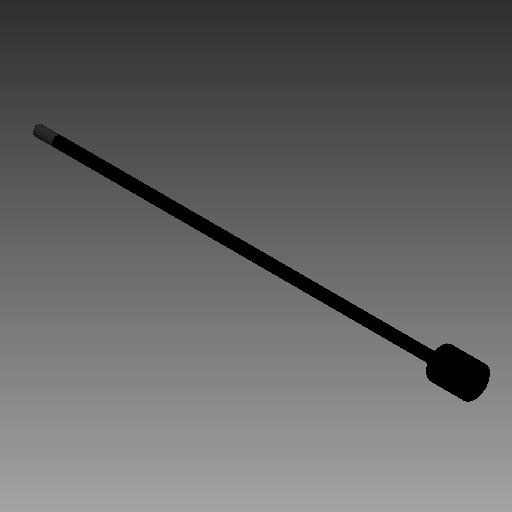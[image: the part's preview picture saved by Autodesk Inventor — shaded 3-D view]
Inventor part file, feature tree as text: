
AUTODESK INVENTOR PART (.ipt)
format: ipt  version: 2019.4 (Build 234330000, 330)  size: 141,312 bytes
history: native  units: in
note: dims shown in document units (in); Inventor stores cm internally (conversion verified against a paired STEP export)
features: other x70, revolve x3, sketch x3, thread x1
ambient origin geometry x8: Origin, YZ Plane, XZ Plane, XY Plane, X Axis, Y Axis, Z Axis, Center Point
bodies: Solid1 (feature_tree)
feature tree (77):
  revolve  "Revolution1"  Angle=360.0deg
  revolve  "Revolution2"  Angle=360.0deg
  thread  "Thread1"  [1 undecoded]
  revolve  "Revolution3"  [1 undecoded]
  other  "dia1_XY"
  other  "dia1_YZ"
  other  "dia1_ZX"
  other  "dia1_X"
  other  "dia1_Y"
  other  "dia1_Z"
  other  "dia1_Center"
  other  "dia12_XY"
  other  "dia12_YZ"
  other  "dia12_ZX"
  other  "dia12_X"
  other  "dia12_Y"
  other  "dia12_Z"
  other  "dia12_Center"
  other  "dia2_XY"
  other  "dia2_YZ"
  other  "dia2_ZX"
  other  "dia2_X"
  other  "dia2_Y"
  other  "dia2_Z"
  other  "dia2_Center"
  other  "dia22_XY"
  other  "dia22_YZ"
  other  "dia22_ZX"
  other  "dia22_X"
  other  "dia22_Y"
  other  "dia22_Z"
  other  "dia22_Center"
  other  "rl1_XY"
  other  "rl1_YZ"
  other  "rl1_ZX"
  other  "rl1_X"
  other  "rl1_Y"
  other  "rl1_Z"
  other  "rl1_Center"
  other  "rl2_XY"
  other  "rl2_YZ"
  other  "rl2_ZX"
  other  "rl2_X"
  other  "rl2_Y"
  other  "rl2_Z"
  other  "rl2_Center"
  other  "rod_cp_XY"
  other  "rod_cp_YZ"
  other  "rod_cp_ZX"
  other  "rod_cp_X"
  other  "rod_cp_Y"
  other  "rod_cp_Z"
  other  "rod_cp_Center"
  other  "thd1_XY"
  other  "thd1_YZ"
  other  "thd1_ZX"
  other  "thd1_X"
  other  "thd1_Y"
  other  "thd1_Z"
  other  "thd1_Center"
  other  "thd2_XY"
  other  "thd2_YZ"
  other  "thd2_ZX"
  other  "thd2_X"
  other  "thd2_Y"
  other  "thd2_Z"
  other  "thd2_Center"
  other  "to_rod_clevis_XY"
  other  "to_rod_clevis_YZ"
  other  "to_rod_clevis_ZX"
  other  "to_rod_clevis_X"
  other  "to_rod_clevis_Y"
  other  "to_rod_clevis_Z"
  other  "to_rod_clevis_Center"
  sketch  "Sketch_1"  dims[d0=360.0deg d1=360.0deg]
  sketch  "Sketch_3"  dims[d2=0.4787in d3=0.0in d4=360.0deg]
  sketch  "Sketch_30"  dims[d5=0.0in d6=0.0in d7=0.0in d8=0.0in d9=0.0in]
note: 2 required parameter values undecoded (feature->parameter linkage not recoverable at this tier; creation-order binding heuristic only, values carry confidence <= 0.55)
